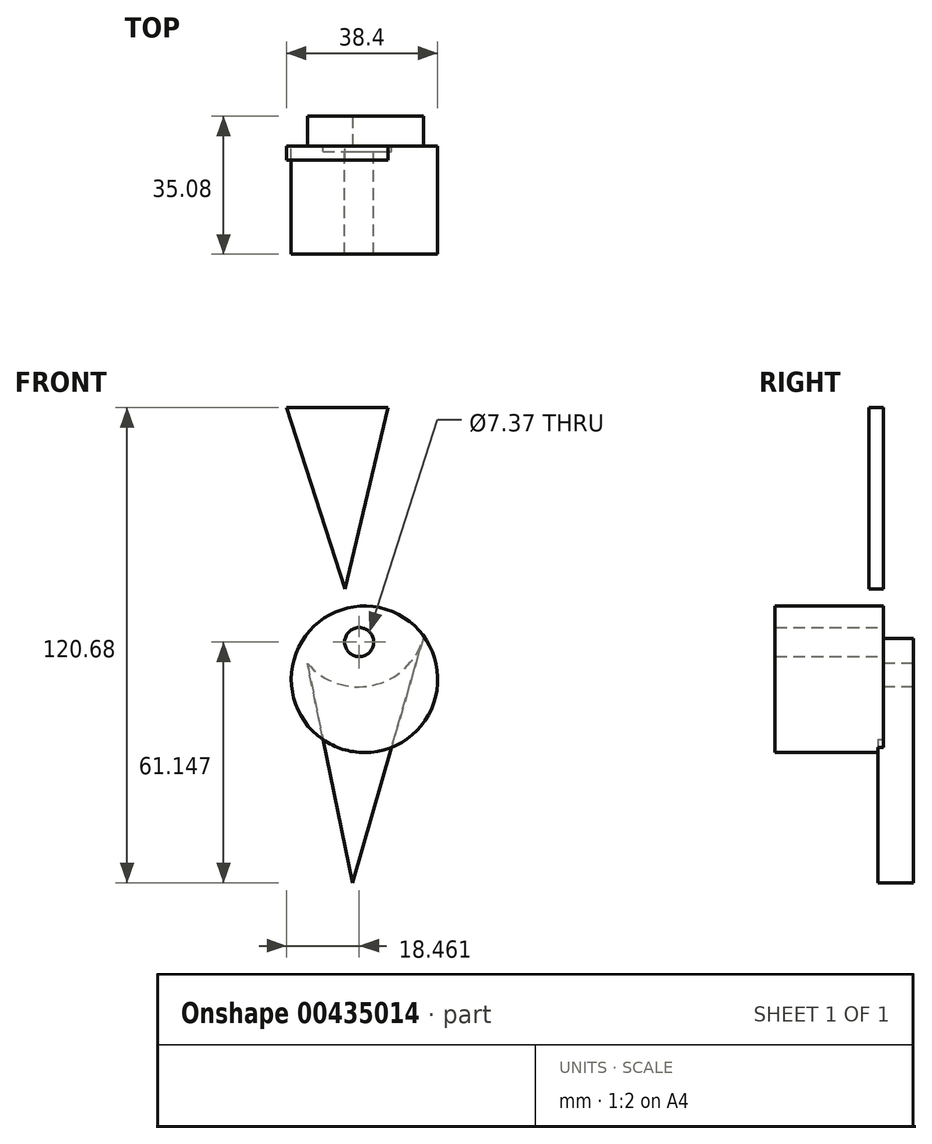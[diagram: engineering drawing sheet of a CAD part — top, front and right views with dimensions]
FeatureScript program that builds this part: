
annotation { "Feature Type Name" : "Feature", "Feature Type Description" : "" }
export const myFeature = defineFeature(function(context is Context, id is Id, definition is map)
    precondition{}
    {
        {
            var Q0;
            Q0=qCreatedBy(makeId("Front.planeOp"),FACE);
            var sketch = newSketch(context, id + "F0", { "sketchPlane" : qUnion([Q0])});
            skLineSegment(sketch, "E0.bottom", {"start": v(-30.86, -83.46) * mm, "end": v(-61.52, -83.46) * mm});
            skLineSegment(sketch, "E0.top", {"start": v(-30.86, 6.66) * mm, "end": v(-61.52, 6.66) * mm});
            skLineSegment(sketch, "E0.left", {"start": v(-30.86, -83.46) * mm, "end": v(-30.86, 6.66) * mm});
            skLineSegment(sketch, "E0.right", {"start": v(-61.52, -83.46) * mm, "end": v(-61.52, 6.66) * mm});
            skPoint(sketch, "E0.middle", {"position": v(-46.2, -38.4) * mm});
            skCircle(sketch, "E1", {"center": v(-46.2, -100.6) * mm, "radius": 17.13 * mm});
            skPoint(sketch, "E1.centerSnap0", {"position": v(-46.2, -83.46) * mm});
            skLineSegment(sketch, "E2", {"start": v(-59.2, -111.73) * mm, "end": v(-47.77, -167.5) * mm});
            skLineSegment(sketch, "E3", {"start": v(-47.77, -167.5) * mm, "end": v(-29.74, -105.36) * mm});
            skSolve(sketch);
        }
        {
            var Q0;
            {var subQ0=sQuery(id+"F0.wireOp",EDGE,"E2");Q0=makeQuery(id+"F0.imprint","IMPRINT",FACE,{"disambiguationData":[TD([[makeQuery(id+"F0.imprint","IMPRINT",EDGE,{"derivedFrom":subQ0}),1.0]])]});}
            extrude(context, id + "F1", {"entities" : qUnion([Q0]), "oppositeDirection" : true, "depth" : 7.54 * mm});
        }
        {
            var Q0;
            Q0=makeQuery(id+"F1.opExtrude","CAP_FACE",FACE,{"disambiguationData":[OSD([sQuery(id+"F0.wireOp",EDGE,"E1"),sQuery(id+"F0.wireOp",EDGE,"E2"),sQuery(id+"F0.wireOp",EDGE,"E3")])],"isStart":true});
            extrude(context, id + "F2", {"entities" : qUnion([Q0]), "operationType" : NewBodyOperationType.ADD, "depth" : 1.43 * mm});
        }
        {
            var Q0;
            Q0=qCreatedBy(makeId("Front.planeOp"),FACE);
            var sketch = newSketch(context, id + "F3", { "sketchPlane" : qUnion([Q0])});
            skCircle(sketch, "E4", {"center": v(-44.68, -115.8) * mm, "radius": 18.6 * mm});
            skSolve(sketch);
        }
        {
            var Q0;
            Q0=makeQuery(id+"F3.imprint","IMPRINT",FACE,{"disambiguationData":[TD([[makeQuery(id+"F3.imprint","IMPRINT",EDGE,{"derivedFrom":sQuery(id+"F3.wireOp",EDGE,"E4")}),1.0]])]});
            extrude(context, id + "F4", {"entities" : qUnion([Q0]), "operationType" : NewBodyOperationType.ADD, "depth" : 27.54 * mm});
        }
        {
            var Q0;
            Q0=qCreatedBy(makeId("Front.planeOp"),FACE);
            var sketch = newSketch(context, id + "F5", { "sketchPlane" : qUnion([Q0])});
            skLineSegment(sketch, "E5", {"start": v(-49.66, -92.9) * mm, "end": v(-64.48, -46.8) * mm});
            skLineSegment(sketch, "E6", {"start": v(-64.48, -46.8) * mm, "end": v(-38.63, -46.8) * mm});
            skLineSegment(sketch, "E7", {"start": v(-38.63, -46.8) * mm, "end": v(-49.66, -92.9) * mm});
            skSolve(sketch);
        }
        {
            var Q0;
            Q0=makeQuery(id+"F5.imprint","IMPRINT",FACE,{"disambiguationData":[TD([[makeQuery(id+"F5.imprint","IMPRINT",EDGE,{"derivedFrom":sQuery(id+"F5.wireOp",EDGE,"E5")}),-1.0]])]});
            extrude(context, id + "F6", {"entities" : qUnion([Q0]), "depth" : 3.67 * mm});
        }
        {
            var Q0;
            Q0=qCreatedBy(makeId("Front.planeOp"),FACE);
            var sketch = newSketch(context, id + "F7", { "sketchPlane" : qUnion([Q0])});
            skPoint(sketch, "E8", {"position": v(-46.02, -106.34) * mm});
            skSolve(sketch);
        }
        {
            var Q0;
            Q0=sQuery(id+"F7.wireOp",VERTEX,"E8");
            var Q1;
            Q1=makeQuery(id+"F1.opExtrude","SWEPT_BODY",BODY,{"disambiguationData":[OSD([sQuery(id+"F0.wireOp",EDGE,"E1"),sQuery(id+"F0.wireOp",EDGE,"E2"),sQuery(id+"F0.wireOp",EDGE,"E3")])]});
            hole(context, id + "F8", {"style" : HoleStyle.SIMPLE, "endStyle" : HoleEndStyle.THROUGH, "oppositeDirection" : true, "holeDiameter" : 7.37 * mm, "isTappedThrough" : true, "tappedDepth" : 12.7 * mm, "tapClearance" : 3, "locations" : qUnion([Q0]), "scope" : qUnion([Q1])});
        }
    });
